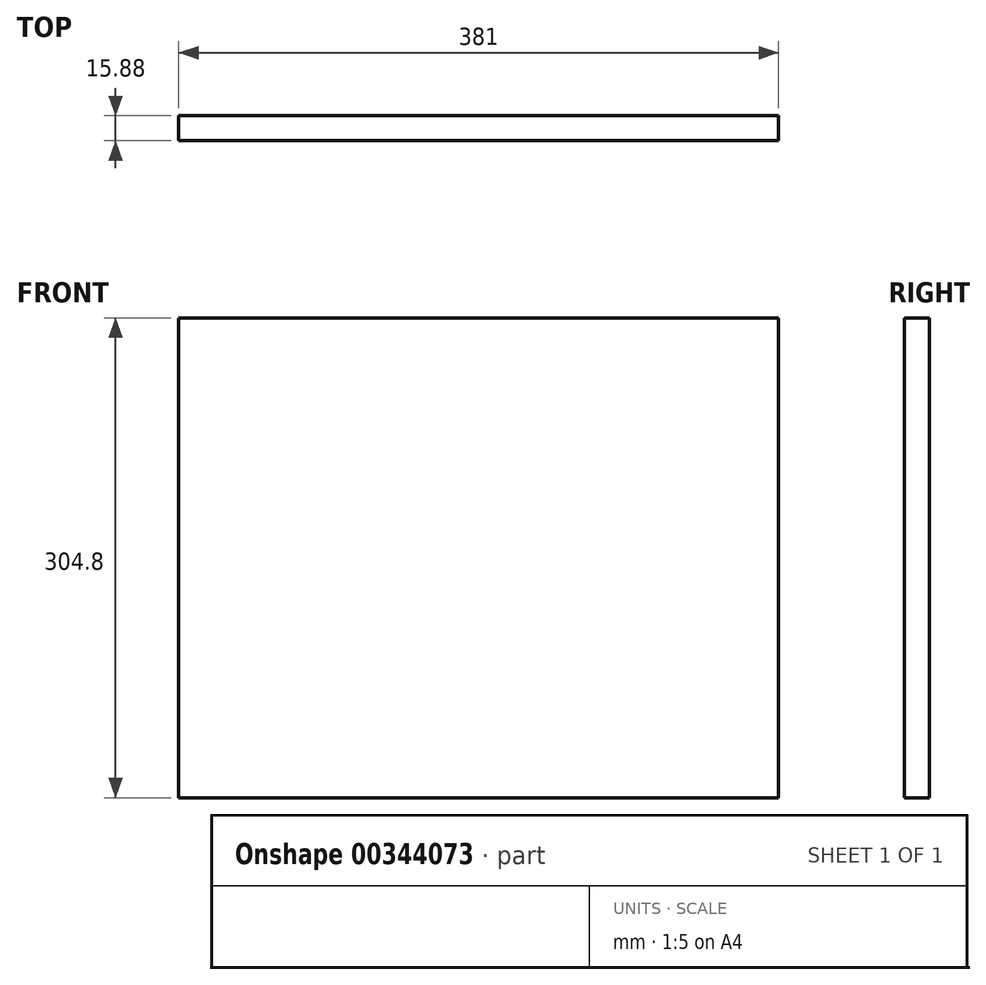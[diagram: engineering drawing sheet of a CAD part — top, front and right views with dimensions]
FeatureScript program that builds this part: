
annotation { "Feature Type Name" : "Feature", "Feature Type Description" : "" }
export const myFeature = defineFeature(function(context is Context, id is Id, definition is map)
    precondition{}
    {
        {
            var Q0;
            Q0=qCreatedBy(makeId("Front.planeOp"),FACE);
            var sketch = newSketch(context, id + "F0", { "sketchPlane" : qUnion([Q0])});
            skLineSegment(sketch, "E0.bottom", {"start": v(0, 0) * mm, "end": v(381, 0) * mm});
            skLineSegment(sketch, "E0.top", {"start": v(0, 304.8) * mm, "end": v(381, 304.8) * mm});
            skLineSegment(sketch, "E0.left", {"start": v(0, 0) * mm, "end": v(0, 304.8) * mm});
            skLineSegment(sketch, "E0.right", {"start": v(381, 0) * mm, "end": v(381, 304.8) * mm});
            skSolve(sketch);
        }
        {
            var Q0;
            Q0=qSketchRegion(id+"F0",true);
            extrude(context, id + "F1", {"entities" : qUnion([Q0]), "depth" : 15.88 * mm});
        }
    });
